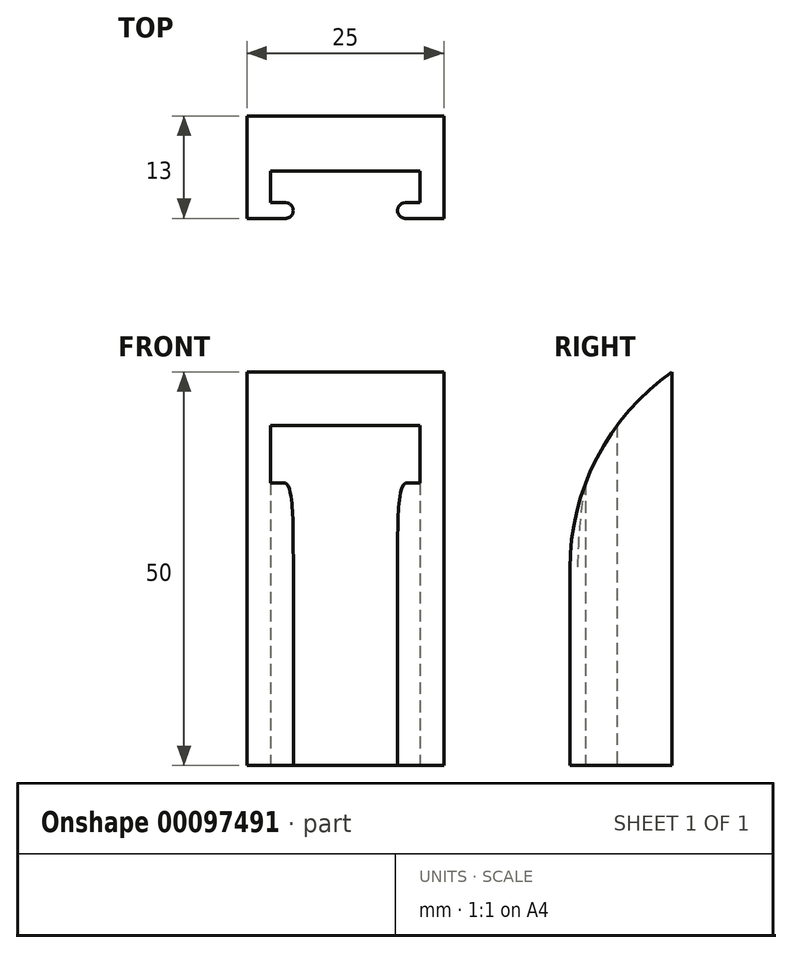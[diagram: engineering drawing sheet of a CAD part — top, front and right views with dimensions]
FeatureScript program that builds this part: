
annotation { "Feature Type Name" : "Feature", "Feature Type Description" : "" }
export const myFeature = defineFeature(function(context is Context, id is Id, definition is map)
    precondition{}
    {
        {
            var Q0;
            Q0=qCreatedBy(makeId("Top.planeOp"),FACE);
            var sketch = newSketch(context, id + "F0", { "sketchPlane" : qUnion([Q0])});
            skLineSegment(sketch, "E0", {"start": v(0, 0) * mm, "end": v(-9.5, 0) * mm});
            skLineSegment(sketch, "E1", {"start": v(0, 0) * mm, "end": v(0, -23.25) * mm, "construction": true});
            skLineSegment(sketch, "E2.MirrorCS", {"start": v(0, 0) * mm, "end": v(9.5, 0) * mm});
            skLineSegment(sketch, "E3", {"start": v(-9.5, 0) * mm, "end": v(-9.5, -4) * mm});
            skLineSegment(sketch, "E4", {"start": v(-9.5, -4) * mm, "end": v(-6.62, -4) * mm});
            skLineSegment(sketch, "E5", {"start": v(-6.62, -4) * mm, "end": v(-6.62, -6) * mm});
            skLineSegment(sketch, "E6", {"start": v(-6.62, -6) * mm, "end": v(-12.5, -6) * mm});
            skLineSegment(sketch, "E7.MirrorCS", {"start": v(9.5, 0) * mm, "end": v(9.5, -4) * mm});
            skLineSegment(sketch, "E8.MirrorCS", {"start": v(9.5, -4) * mm, "end": v(6.62, -4) * mm});
            skLineSegment(sketch, "E9.MirrorCS", {"start": v(6.63, -4) * mm, "end": v(6.63, -6) * mm});
            skLineSegment(sketch, "E10.MirrorCS", {"start": v(6.62, -6) * mm, "end": v(12.5, -6) * mm});
            skLineSegment(sketch, "E11", {"start": v(-12.5, -6) * mm, "end": v(-12.5, 7) * mm});
            skLineSegment(sketch, "E12", {"start": v(-12.5, 7) * mm, "end": v(0, 7) * mm});
            skLineSegment(sketch, "E13.MirrorCS", {"start": v(12.5, -6) * mm, "end": v(12.5, 7) * mm});
            skLineSegment(sketch, "E14.MirrorCS", {"start": v(12.5, 7) * mm, "end": v(0, 7) * mm});
            skSolve(sketch);
        }
        {
            var Q0;
            Q0=makeQuery(id+"F0.imprint","IMPRINT",FACE,{"disambiguationData":[TD([[makeQuery(id+"F0.imprint","IMPRINT",EDGE,{"derivedFrom":sQuery(id+"F0.wireOp",EDGE,"E0")}),-1.0]])]});
            extrude(context, id + "F1", {"entities" : qUnion([Q0]), "depth" : 50 * mm});
        }
        {
            var Q0;
            Q0=makeQuery(id+"F1.opExtrude","SWEPT_FACE",FACE,{"disambiguationData":[OSD([sQuery(id+"F0.wireOp",EDGE,"E13.MirrorCS")])]});
            var sketch = newSketch(context, id + "F2", { "sketchPlane" : qUnion([Q0])});
            skArc(sketch, "E15", {"start": v(7, 50) * mm, "mid": v(-2.56, 39.09) * mm, "end": v(-6, 25) * mm});
            skSolve(sketch);
        }
        {
            var Q0;
            {var subQ0=sQuery(id+"F2.wireOp",EDGE,"E15");Q0=makeQuery(id+"F2.imprint","IMPRINT",FACE,{"disambiguationData":[TD([[makeQuery(id+"F2.imprint","IMPRINT",EDGE,{"derivedFrom":subQ0}),-1.0]])]});}
            var Q1;
            Q1=makeQuery(id+"F1.opExtrude","SWEPT_FACE",FACE,{"disambiguationData":[OSD([sQuery(id+"F0.wireOp",EDGE,"E11")])]});
            extrude(context, id + "F3", {"entities" : qUnion([Q0]), "operationType" : NewBodyOperationType.REMOVE, "endBound" : BoundingType.UP_TO_SURFACE, "oppositeDirection" : true, "endBoundEntityFace" : qUnion([Q1]), "depth" : 25 * mm});
        }
        {
            var Q0;
            Q0=makeQuery(id+"F1.opExtrude","SWEPT_EDGE",EDGE,{"disambiguationData":[OSD([sQuery(id+"F0.wireOp",EDGE,"E5"),sQuery(id+"F0.wireOp",EDGE,"E6")])]});
            var Q1;
            Q1=makeQuery(id+"F1.opExtrude","SWEPT_EDGE",EDGE,{"disambiguationData":[OSD([sQuery(id+"F0.wireOp",EDGE,"E4"),sQuery(id+"F0.wireOp",EDGE,"E5")])]});
            var Q2;
            Q2=makeQuery(id+"F1.opExtrude","SWEPT_EDGE",EDGE,{"disambiguationData":[OSD([sQuery(id+"F0.wireOp",EDGE,"E9.MirrorCS"),sQuery(id+"F0.wireOp",EDGE,"E10.MirrorCS")])]});
            var Q3;
            Q3=makeQuery(id+"F1.opExtrude","SWEPT_EDGE",EDGE,{"disambiguationData":[OSD([sQuery(id+"F0.wireOp",EDGE,"E8.MirrorCS"),sQuery(id+"F0.wireOp",EDGE,"E9.MirrorCS")])]});
            var Q4;
            Q4=makeQuery(id+"F3.boolean.opBoolean","COPY",EDGE,{"derivedFrom":makeQuery(id+"F3.opExtrude","CAP_EDGE",EDGE,{"disambiguationData":[OSD([sQuery(id+"F2.wireOp",EDGE,"E15")])],"isStart":false})});
            var Q5;
            Q5=makeQuery(id+"F3.boolean.opBoolean","COPY",EDGE,{"derivedFrom":makeQuery(id+"F3.opExtrude","CAP_EDGE",EDGE,{"disambiguationData":[OSD([sQuery(id+"F2.wireOp",EDGE,"E15")])],"isStart":true})});
            fillet(context, id + "F4", {"entities" : qUnion([Q0, Q1, Q2, Q3, Q4, Q5]), "radius" : 1 * mm, "tangentPropagation" : true, "allowEdgeOverflow" : false});
        }
    });
